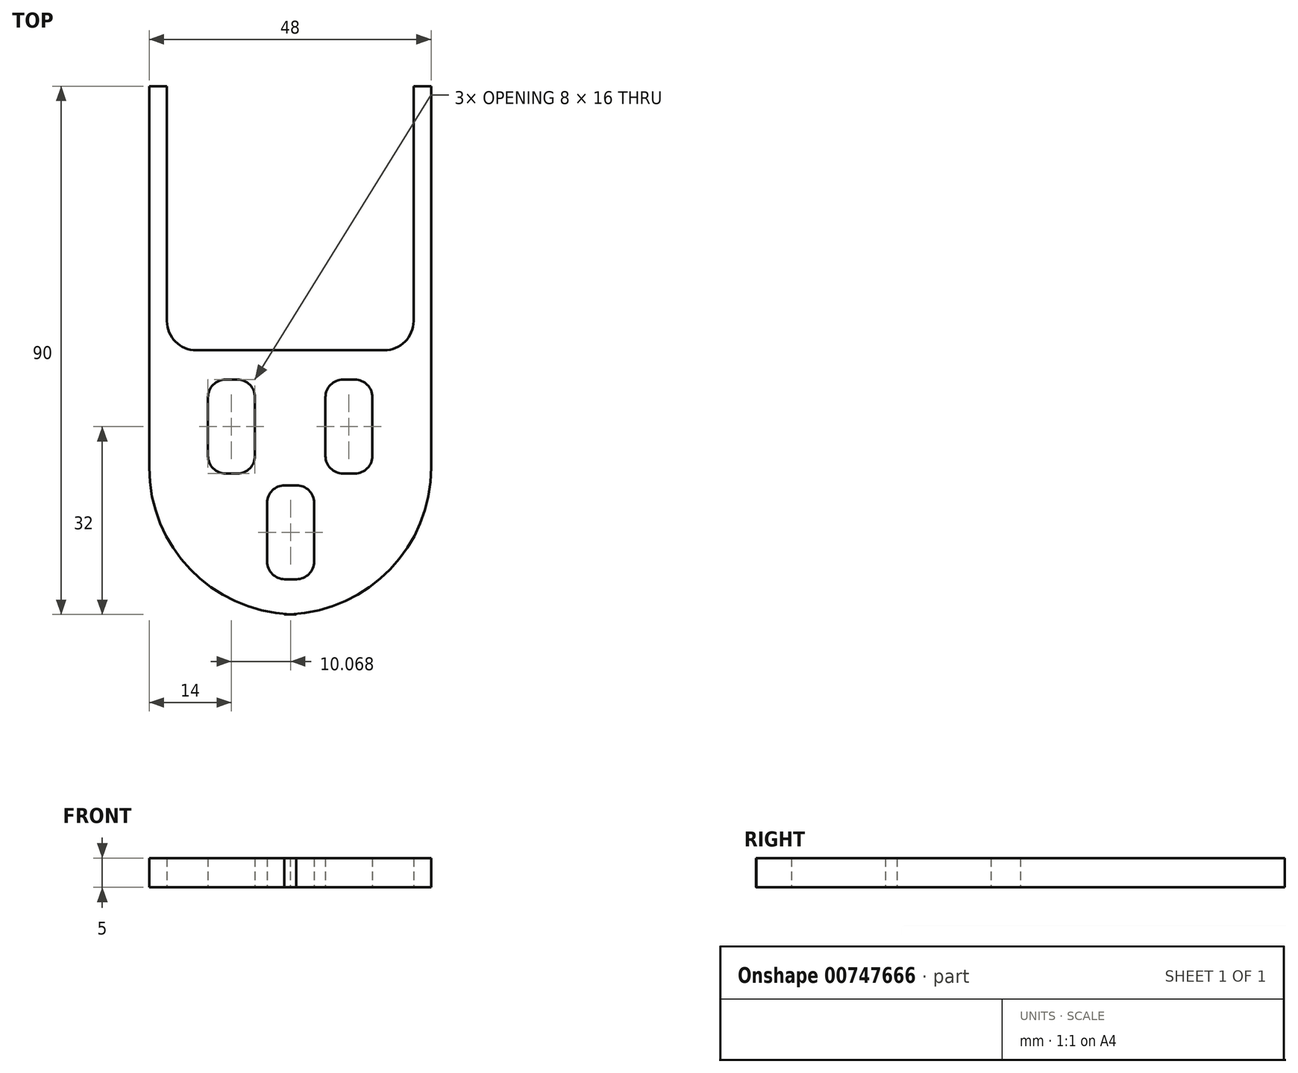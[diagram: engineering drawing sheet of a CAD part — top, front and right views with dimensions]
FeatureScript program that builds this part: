
annotation { "Feature Type Name" : "Feature", "Feature Type Description" : "" }
export const myFeature = defineFeature(function(context is Context, id is Id, definition is map)
    precondition{}
    {
        {
            var Q0;
            Q0=qCreatedBy(makeId("Top.planeOp"),FACE);
            var sketch = newSketch(context, id + "F0", { "sketchPlane" : qUnion([Q0])});
            skLineSegment(sketch, "E0.bottom", {"start": v(-24, 45) * mm, "end": v(-21, 45) * mm});
            skLineSegment(sketch, "E0.top", {"start": v(-1, -45) * mm, "end": v(1, -45) * mm});
            skLineSegment(sketch, "E0.left", {"start": v(-24, 45) * mm, "end": v(-24, -20) * mm});
            skLineSegment(sketch, "E0.right", {"start": v(24, 45) * mm, "end": v(24, -20) * mm});
            skLineSegment(sketch, "E1.top", {"start": v(-16, 0) * mm, "end": v(16, 0) * mm});
            skLineSegment(sketch, "E1.left", {"start": v(-21, 45) * mm, "end": v(-21, 5) * mm});
            skLineSegment(sketch, "E1.right", {"start": v(21, 45) * mm, "end": v(21, 5) * mm});
            skLineSegment(sketch, "E2", {"start": v(21, 45) * mm, "end": v(24, 45) * mm});
            skLineSegment(sketch, "E3.bottom", {"start": v(-11, -5) * mm, "end": v(-9, -5) * mm});
            skLineSegment(sketch, "E3.top", {"start": v(-11, -21) * mm, "end": v(-9, -21) * mm});
            skLineSegment(sketch, "E3.left", {"start": v(-14, -8) * mm, "end": v(-14, -18) * mm});
            skLineSegment(sketch, "E3.right", {"start": v(-6, -8) * mm, "end": v(-6, -18) * mm});
            skPoint(sketch, "E4.visualSharp", {"position": v(-14, -5) * mm});
            skArc(sketch, "E4.filletArc", {"start": v(-11, -5) * mm, "mid": v(-13.12, -5.88) * mm, "end": v(-14, -8) * mm});
            skPoint(sketch, "E5.visualSharp", {"position": v(-14, -21) * mm});
            skArc(sketch, "E5.filletArc", {"start": v(-14, -18) * mm, "mid": v(-13.12, -20.12) * mm, "end": v(-11, -21) * mm});
            skPoint(sketch, "E6.visualSharp", {"position": v(-6, -5) * mm});
            skArc(sketch, "E6.filletArc", {"start": v(-6, -8) * mm, "mid": v(-6.88, -5.88) * mm, "end": v(-9, -5) * mm});
            skPoint(sketch, "E7.visualSharp", {"position": v(-6, -21) * mm});
            skArc(sketch, "E7.filletArc", {"start": v(-9, -21) * mm, "mid": v(-6.88, -20.12) * mm, "end": v(-6, -18) * mm});
            skLineSegment(sketch, "E8", {"start": v(0, 0) * mm, "end": v(0, -45) * mm, "construction": true});
            skLineSegment(sketch, "E9.MirrorCS", {"start": v(6, -8) * mm, "end": v(6, -18) * mm});
            skArc(sketch, "E10.MirrorCS", {"start": v(6, -8) * mm, "mid": v(6.88, -5.88) * mm, "end": v(9, -5) * mm});
            skLineSegment(sketch, "E11.MirrorCS", {"start": v(11, -5) * mm, "end": v(9, -5) * mm});
            skArc(sketch, "E12.MirrorCS", {"start": v(11, -5) * mm, "mid": v(13.12, -5.88) * mm, "end": v(14, -8) * mm});
            skLineSegment(sketch, "E13.MirrorCS", {"start": v(14, -8) * mm, "end": v(14, -18) * mm});
            skArc(sketch, "E14.MirrorCS", {"start": v(14, -18) * mm, "mid": v(13.12, -20.12) * mm, "end": v(11, -21) * mm});
            skLineSegment(sketch, "E15.MirrorCS", {"start": v(11, -21) * mm, "end": v(9, -21) * mm});
            skArc(sketch, "E16.MirrorCS", {"start": v(9, -21) * mm, "mid": v(6.88, -20.12) * mm, "end": v(6, -18) * mm});
            skLineSegment(sketch, "E17.bottom", {"start": v(-0.93, -23) * mm, "end": v(1.07, -23) * mm});
            skLineSegment(sketch, "E17.top", {"start": v(-0.93, -39) * mm, "end": v(1.07, -39) * mm});
            skLineSegment(sketch, "E17.left", {"start": v(-3.93, -26) * mm, "end": v(-3.93, -36) * mm});
            skLineSegment(sketch, "E17.right", {"start": v(4.07, -26) * mm, "end": v(4.07, -36) * mm});
            skArc(sketch, "E18.filletArc", {"start": v(-0.93, -23) * mm, "mid": v(-3.05, -23.88) * mm, "end": v(-3.93, -26) * mm});
            skArc(sketch, "E19.filletArc", {"start": v(-3.93, -36) * mm, "mid": v(-3.05, -38.12) * mm, "end": v(-0.93, -39) * mm});
            skArc(sketch, "E20.filletArc", {"start": v(4.07, -26) * mm, "mid": v(3.19, -23.88) * mm, "end": v(1.07, -23) * mm});
            skArc(sketch, "E21.filletArc", {"start": v(1.07, -39) * mm, "mid": v(3.19, -38.12) * mm, "end": v(4.07, -36) * mm});
            skPoint(sketch, "E22.visualSharp", {"position": v(-21, 0) * mm});
            skArc(sketch, "E22.filletArc", {"start": v(-21, 5) * mm, "mid": v(-19.54, 1.46) * mm, "end": v(-16, 0) * mm});
            skPoint(sketch, "E23.visualSharp", {"position": v(21, 0) * mm});
            skArc(sketch, "E23.filletArc", {"start": v(16, 0) * mm, "mid": v(19.54, 1.46) * mm, "end": v(21, 5) * mm});
            skPoint(sketch, "E24.visualSharp", {"position": v(-24, -45) * mm});
            skArc(sketch, "E24.filletArc", {"start": v(-24, -20) * mm, "mid": v(-16.68, -37.68) * mm, "end": v(1, -45) * mm});
            skPoint(sketch, "E25.visualSharp", {"position": v(24, -45) * mm});
            skArc(sketch, "E25.filletArc", {"start": v(-1, -45) * mm, "mid": v(16.68, -37.68) * mm, "end": v(24, -20) * mm});
            skSolve(sketch);
        }
        {
            var Q0;
            Q0 = qSketchRegion(id + "F0", true);
            extrude(context, id + "F1", {"entities" : qUnion([Q0]), "depth" : 5 * mm, "offsetDistance" : 25 * mm});
        }
    });
